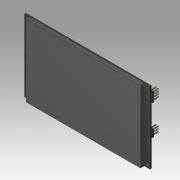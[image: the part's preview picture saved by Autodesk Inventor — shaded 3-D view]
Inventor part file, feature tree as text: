
AUTODESK INVENTOR PART (.ipt)
format: ipt  version: 2019.3 (Build 233278000, 278)  size: 436,224 bytes
history: native  units: mm
features: extrude x12, sketch x12, projected_geometry x8
ambient origin geometry x8: Origin, YZ Plane, XZ Plane, XY Plane, X Axis, Y Axis, Z Axis, Center Point
bodies: Solid1 (feature_tree)
feature tree (32):
  extrude  "Extrusion1"  Depth=76.0mm
  extrude  "Extrusion2"  Depth=70.6mm
  extrude  "Extrusion3"  Depth=2.7mm
  extrude  "Extrusion4"  Depth=2.7mm
  extrude  "Extrusion5"  Depth=1.6mm TaperAngle=0.0deg
  extrude  "Extrusion6"  Depth=75.999mm
  extrude  "Extrusion7"  Depth=4.0mm TaperAngle=0.0deg
  extrude  "Extrusion8"  Depth=7.5mm
  extrude  "Extrusion9"  Depth=10.0mm
  extrude  "Extrusion10"  Depth=24.5mm
  extrude  "Extrusion11"  Depth=0.01mm
  extrude  "Extrusion12"  Depth=20.0mm
  sketch  "Sketch1"  dims[d0=133.0mm d1=76.0mm]
  sketch  "Sketch2"  dims[d2=3.1mm d3=70.6mm]
  projected_geometry  "Projected Loop1"
  sketch  "Sketch3"  dims[d4=127.6mm d5=2.7mm]
  sketch  "Sketch4"  dims[d6=2.7mm d7=2.7mm]
  sketch  "Sketch5"  dims[d8=2.7mm d9=1.6mm d10=0.0mm]
  sketch  "Sketch6"  dims[d11=121.0mm d12=75.999mm]
  sketch  "Sketch7"  dims[d13=6.0mm d14=4.0mm d15=0.0mm]
  sketch  "Sketch8"  dims[d16=5.0mm d17=7.5mm]
  projected_geometry  "Projected Loop2"
  projected_geometry  "Projected Loop3"
  projected_geometry  "Projected Loop4"
  projected_geometry  "Projected Loop5"
  sketch  "Sketch9"  dims[d18=5.0mm d19=10.0mm]
  projected_geometry  "Projected Loop6"
  sketch  "Sketch10"  dims[d20=6.5mm d21=24.5mm]
  sketch  "Sketch11"  dims[d22=27.5mm d23=0.01mm]
  projected_geometry  "Projected Loop7"
  sketch  "Sketch12"  dims[d24=2.5mm d25=0.0mm d26=20.0mm d28=2.54mm d29=40.0mm d31=2.54mm d34=0.815mm d35=0.75mm d36=0.75mm d37=0.855mm d38=0.855mm d39=0.815mm d40=20.0mm d42=2.54mm d43=30.0mm d45=2.54mm d48=0.86mm d49=0.81mm d50=6.0mm d51=0.0mm d52=14.0mm d53=14.0mm d54=24.0mm d55=39.0mm d56=1.4mm d57=0.0mm d58=6.1mm d59=10.0mm d60=5.0mm d61=22.0mm d62=6.0mm d63=0.0mm d64=13.0mm d65=36.0mm d66=4.0mm d67=16.0mm d68=7.0mm d69=2.5mm d70=10.5mm d71=7.0mm d72=2.5mm d73=0.0mm d74=1.3mm d75=15.0mm d76=37.0mm d77=2.45mm d78=0.0mm d79=3.5mm d80=10.0mm d81=23.0mm d82=36.0mm d83=3.5mm d84=0.0mm d85=24.5mm d86=29.0mm d87=29.0mm d88=25.5mm d89=15.0mm d90=15.0mm d91=3.5mm d92=18.0mm d93=2.0mm d94=0.0mm d95=20.0mm d96=20.0mm d97=48.0mm d98=0.2mm d99=0.0mm d100=0.2mm d101=0.0mm]
  projected_geometry  "Projected Loop8"
